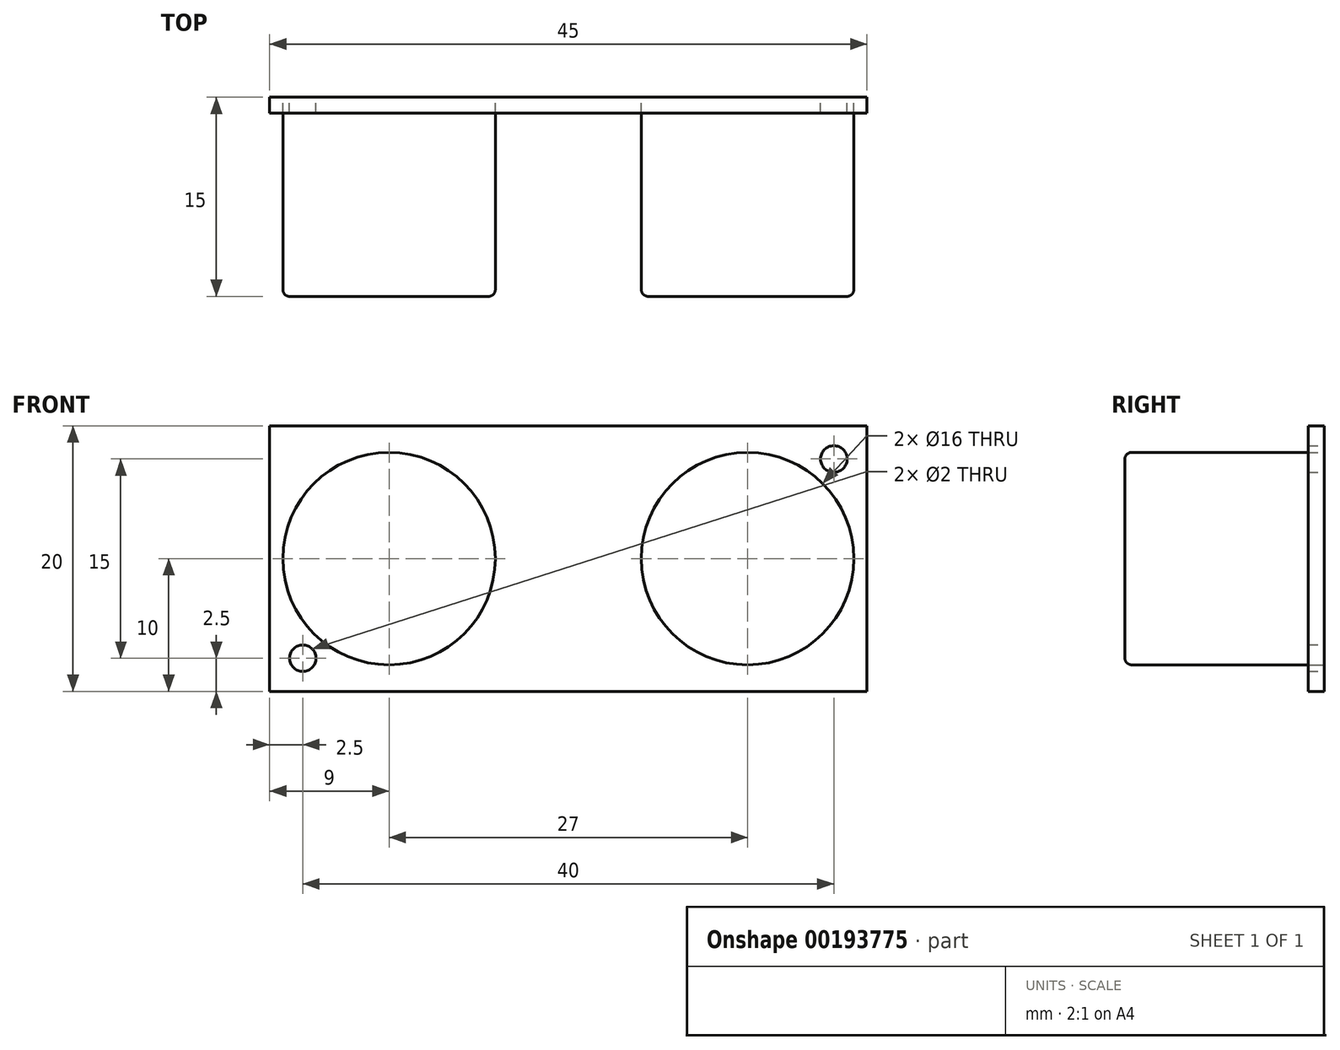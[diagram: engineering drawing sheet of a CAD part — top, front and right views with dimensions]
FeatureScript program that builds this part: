
annotation { "Feature Type Name" : "Feature", "Feature Type Description" : "" }
export const myFeature = defineFeature(function(context is Context, id is Id, definition is map)
    precondition{}
    {
        {
            var Q0;
            Q0=qCreatedBy(makeId("Front.planeOp"),FACE);
            var sketch = newSketch(context, id + "F0", { "sketchPlane" : qUnion([Q0])});
            skCircle(sketch, "E0", {"center": v(-13.5, 0) * mm, "radius": 8 * mm});
            skCircle(sketch, "E1.1.0.0", {"center": v(13.5, 0) * mm, "radius": 8 * mm});
            skLineSegment(sketch, "E1.direction1", {"start": v(-13.5, 0) * mm, "end": v(13.5, 0) * mm, "construction": true});
            skLineSegment(sketch, "E2.bottom", {"start": v(-22.5, 10) * mm, "end": v(22.5, 10) * mm});
            skLineSegment(sketch, "E2.top", {"start": v(-22.5, -10) * mm, "end": v(22.5, -10) * mm});
            skLineSegment(sketch, "E2.left", {"start": v(-22.5, 10) * mm, "end": v(-22.5, -10) * mm});
            skLineSegment(sketch, "E2.right", {"start": v(22.5, 10) * mm, "end": v(22.5, -10) * mm});
            skPoint(sketch, "E2.middle", {"position": v(0, 0) * mm});
            skCircle(sketch, "E3", {"center": v(20, 7.5) * mm, "radius": 1 * mm});
            skCircle(sketch, "E4", {"center": v(-20, -7.5) * mm, "radius": 1 * mm});
            skSolve(sketch);
        }
        {
            var Q0;
            Q0=makeQuery(id+"F0.imprint","IMPRINT",FACE,{"disambiguationData":[TD([[makeQuery(id+"F0.imprint","IMPRINT",EDGE,{"derivedFrom":sQuery(id+"F0.wireOp",EDGE,"E0")}),1.0]])]});
            var Q1;
            Q1=makeQuery(id+"F0.imprint","IMPRINT",FACE,{"disambiguationData":[TD([[makeQuery(id+"F0.imprint","IMPRINT",EDGE,{"derivedFrom":sQuery(id+"F0.wireOp",EDGE,"E1.1.0.0")}),1.0]])]});
            extrude(context, id + "F1", {"entities" : qUnion([Q0, Q1]), "depth" : 15 * mm});
        }
        {
            var Q0;
            Q0=makeQuery(id+"F0.imprint","IMPRINT",FACE,{"disambiguationData":[TD([[makeQuery(id+"F0.imprint","IMPRINT",EDGE,{"derivedFrom":sQuery(id+"F0.wireOp",EDGE,"E0")}),-1.0]])]});
            extrude(context, id + "F2", {"entities" : qUnion([Q0]), "depth" : 1.2 * mm});
        }
        {
            var Q0;
            Q0=makeQuery(id+"F1.opExtrude","CAP_EDGE",EDGE,{"disambiguationData":[OSD([sQuery(id+"F0.wireOp",EDGE,"E0")])],"isStart":false});
            var Q1;
            Q1=makeQuery(id+"F1.opExtrude","CAP_EDGE",EDGE,{"disambiguationData":[OSD([sQuery(id+"F0.wireOp",EDGE,"E1.1.0.0")])],"isStart":false});
            fillet(context, id + "F3", {"entities" : qUnion([Q0, Q1]), "radius" : 0.5 * mm, "tangentPropagation" : true, "allowEdgeOverflow" : false});
        }
    });
